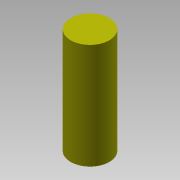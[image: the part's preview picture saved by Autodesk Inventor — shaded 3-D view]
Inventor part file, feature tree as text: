
AUTODESK INVENTOR PART (.ipt)
format: ipt  version: 2015 SP1 (Build 190203100, 203)  size: 83,456 bytes
history: native  units: mm
features: extrude x1, sketch x1
ambient origin geometry x8: Origin, YZ Plane, XZ Plane, XY Plane, X Axis, Y Axis, Z Axis, Center Point
bodies: Solid1 (feature_tree)
feature tree (2):
  extrude  "Extrusion1"  Depth=300.0mm TaperAngle=0.0deg
  sketch  "Sketch1"  dims[d0=110.0mm d1=300.0mm d2=0.0mm]
